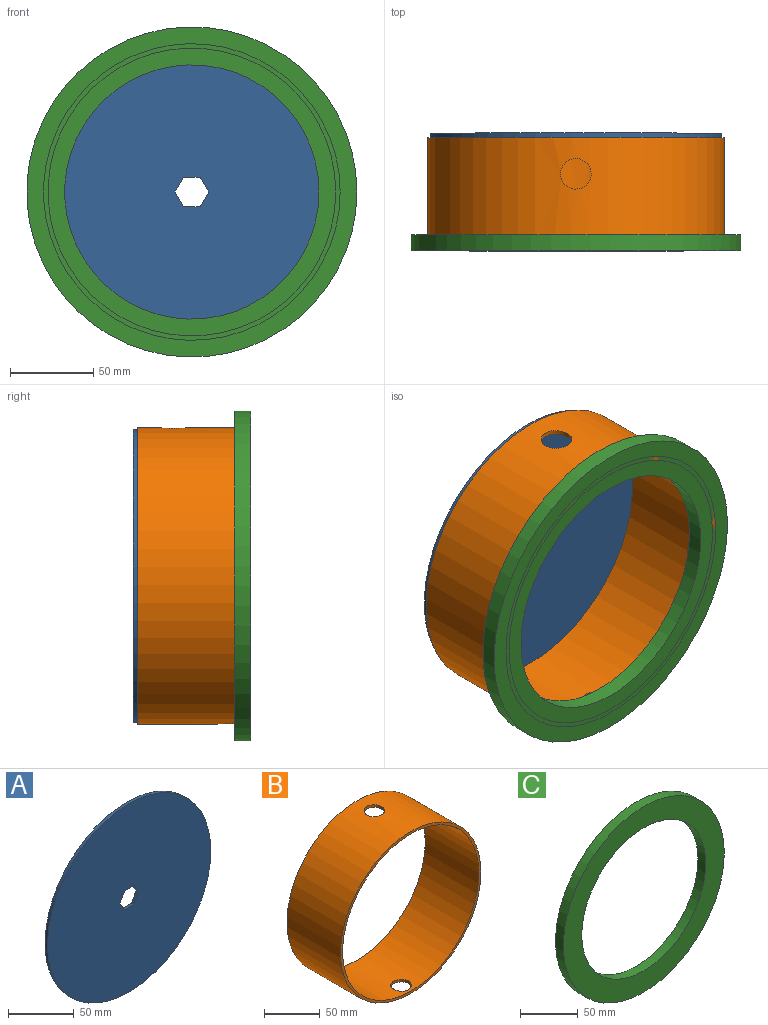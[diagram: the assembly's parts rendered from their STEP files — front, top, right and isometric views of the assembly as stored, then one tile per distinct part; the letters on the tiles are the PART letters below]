
ASSEMBLY  parts=3 mates=2
PART A: 9 faces, bbox 175.1x2.7x175.1 mm
  f0: plane 8.7x5.02mm, normal (-0.87,0,-0.5), area 26.8mm2, adj f1,f5,f7,f8
  f1: plane 8.7x5.02mm, normal (-0.87,0,0.5), area 26.8mm2, adj f0,f2,f7,f8
  f2: plane 10.05x2.67mm, normal (0,0,1), area 26.8mm2, adj f1,f3,f7,f8
  f3: plane 8.7x5.02mm, normal (0.87,0,0.5), area 26.8mm2, adj f2,f4,f7,f8
  f4: plane 8.7x5.02mm, normal (0.87,0,-0.5), area 26.8mm2, adj f3,f5,f7,f8
  f5: plane 10.05x2.67mm, normal (0,0,-1), area 26.8mm2, adj f0,f4,f7,f8
  f6: cylinder r=87.57mm len=175.13mm, axis (0,1,0), area 1467.4mm2, adj f7,f8
  f7: plane 175.13x175.13mm, normal (0,-1,0), area 23827.2mm2, adj f0,f1,f2,f3,f4,f5,f6
  f8: plane 175.13x175.13mm, normal (0,1,0), area 23827.2mm2, adj f0,f1,f2,f3,f4,f5,f6
PART B: 6 faces, bbox 177.8x67.8x177.8 mm
  f0: cylinder r=86.23mm len=172.47mm, axis (0,1,0), area 36217.8mm2, adj f2,f3,f4,f5
  f1: cylinder r=88.9mm len=177.8mm, axis (0,1,0), area 37354.3mm2, adj f2,f3,f4,f5
  f2: plane 177.8x177.8mm, normal (0,-1,0), area 1467.4mm2, adj f0,f1
  f3: plane 177.8x177.8mm, normal (0,1,0), area 1467.4mm2, adj f0,f1
  f4: cylinder r=9.14mm len=18.29mm, axis (0,0,-1), area 153.6mm2, adj f0,f1
  f5: cylinder r=9.14mm len=18.29mm, axis (0,0,1), area 153.6mm2, adj f0,f1
PART C: 4 faces, bbox 197.9x9.5x197.9 mm
  f0: cylinder r=76.2mm len=152.4mm, axis (0,1,0), area 4560.4mm2, adj f2,f3
  f1: cylinder r=98.93mm len=197.87mm, axis (0,1,0), area 5920.9mm2, adj f2,f3
  f2: plane 197.87x197.87mm, normal (0,-1,0), area 12507.6mm2, adj f0,f1
  f3: plane 197.87x197.87mm, normal (0,1,0), area 12507.6mm2, adj f0,f1
PLACE A t=(0.05,1.6,0.35)mm
PLACE B t=(0.05,-1.07,0.35)mm
PLACE C t=(0.05,-59.36,0.35)mm
MATE revolute C.f0 <-> B.f0  axis (0,-1,0) through (0.05,-68.89,0.35)mm
MATE revolute B.f0 <-> A.f6  axis (0,1,0) through (0.05,-1.07,0.35)mm
